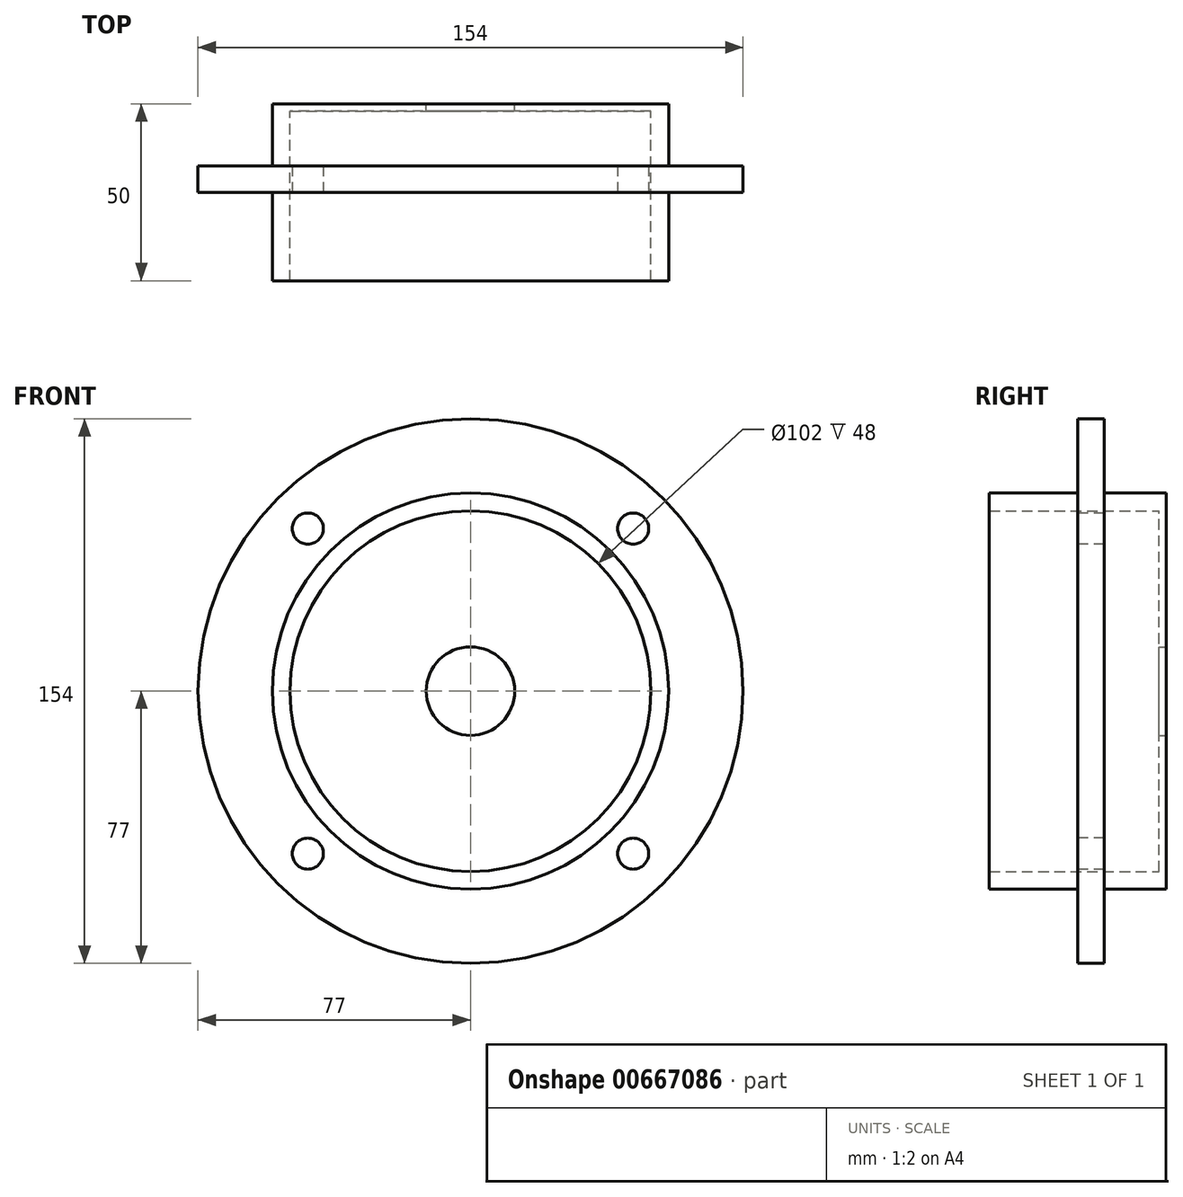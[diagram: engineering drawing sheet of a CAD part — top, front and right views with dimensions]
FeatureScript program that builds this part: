
annotation { "Feature Type Name" : "Feature", "Feature Type Description" : "" }
export const myFeature = defineFeature(function(context is Context, id is Id, definition is map)
    precondition{}
    {
        {
            var Q0;
            Q0=qCreatedBy(makeId("Front.planeOp"),FACE);
            var sketch = newSketch(context, id + "F0", { "sketchPlane" : qUnion([Q0])});
            skCircle(sketch, "E0", {"center": v(0, 0) * mm, "radius": 77 * mm});
            skCircle(sketch, "E1", {"center": v(0, 0) * mm, "radius": 56 * mm});
            skCircle(sketch, "E2.0", {"center": v(0, 0) * mm, "radius": 51 * mm});
            skSolve(sketch);
        }
        {
            var Q0;
            Q0=makeQuery(id+"F0.imprint","IMPRINT",FACE,{"disambiguationData":[TD([[makeQuery(id+"F0.imprint","IMPRINT",EDGE,{"derivedFrom":sQuery(id+"F0.wireOp",EDGE,"E1")}),1.0]])]});
            extrude(context, id + "F1", {"entities" : qUnion([Q0]), "depth" : 50 * mm, "offsetDistance" : 25 * mm});
        }
        {
            var Q0;
            Q0=makeQuery(id+"F0.imprint","IMPRINT",FACE,{"disambiguationData":[TD([[makeQuery(id+"F0.imprint","IMPRINT",EDGE,{"derivedFrom":sQuery(id+"F0.wireOp",EDGE,"E0")}),1.0]])]});
            extrude(context, id + "F2", {"entities" : qUnion([Q0]), "operationType" : NewBodyOperationType.ADD, "depth" : 25 * mm, "offsetDistance" : 25 * mm});
        }
        {
            var Q0;
            Q0=makeQuery(id+"F0.imprint","IMPRINT",FACE,{"disambiguationData":[TD([[makeQuery(id+"F0.imprint","IMPRINT",EDGE,{"derivedFrom":sQuery(id+"F0.wireOp",EDGE,"E0")}),1.0]])]});
            extrude(context, id + "F3", {"entities" : qUnion([Q0]), "operationType" : NewBodyOperationType.REMOVE, "depth" : 17.5 * mm, "offsetDistance" : 25 * mm});
        }
        {
            var Q0;
            Q0=makeQuery(id+"F2.opExtrude","CAP_FACE",FACE,{"disambiguationData":[OSD([sQuery(id+"F0.wireOp",EDGE,"E0"),sQuery(id+"F0.wireOp",EDGE,"E1")])],"isStart":false});
            var sketch = newSketch(context, id + "F4", { "sketchPlane" : qUnion([Q0])});
            skPoint(sketch, "E3", {"position": v(-45.96, 45.96) * mm});
            skPoint(sketch, "E4", {"position": v(45.96, 45.96) * mm});
            skPoint(sketch, "E5", {"position": v(45.96, -45.96) * mm});
            skPoint(sketch, "E6", {"position": v(-45.96, -45.96) * mm});
            skSolve(sketch);
        }
        {
            var Q0;
            Q0=sQuery(id+"F4.wireOp",VERTEX,"E3");
            var Q1;
            Q1=sQuery(id+"F4.wireOp",VERTEX,"E4");
            var Q2;
            Q2=sQuery(id+"F4.wireOp",VERTEX,"E5");
            var Q3;
            Q3=sQuery(id+"F4.wireOp",VERTEX,"E6");
            var Q4;
            Q4=makeQuery(id+"F1.opExtrude","SWEPT_BODY",BODY,{"disambiguationData":[OSD([sQuery(id+"F0.wireOp",EDGE,"E1"),sQuery(id+"F0.wireOp",EDGE,"E2.0")])]});
            hole(context, id + "F5", {"style" : HoleStyle.SIMPLE, "endStyle" : HoleEndStyle.THROUGH, "standardTappedOrClearance" : lookupTablePath({ "standard" : "ISO", "fit" : "Normal", "size" : "M8", "type" : "Clearance" }), "standardBlindInLast" : lookupTablePath({ "fit" : "Standard", "standard" : "ISO", "size" : "M8", "type" : "Clearance" }), "holeDiameter" : 8.8 * mm, "majorDiameter" : 5 * mm, "isTappedThrough" : true, "tappedDepth" : 12 * mm, "tapClearance" : 3, "locations" : qUnion([Q0, Q1, Q2, Q3]), "scope" : qUnion([Q4])});
        }
        {
            var Q0;
            Q0=qCreatedBy(makeId("Front.planeOp"),FACE);
            var sketch = newSketch(context, id + "F6", { "sketchPlane" : qUnion([Q0])});
            skCircle(sketch, "E7", {"center": v(0, 0) * mm, "radius": 12.5 * mm});
            skCircle(sketch, "E8.0", {"center": v(0, 0) * mm, "radius": 51 * mm});
            skSolve(sketch);
        }
        {
            var Q0;
            Q0=makeQuery(id+"F6.imprint","IMPRINT",FACE,{"disambiguationData":[TD([[makeQuery(id+"F6.imprint","IMPRINT",EDGE,{"derivedFrom":sQuery(id+"F6.wireOp",EDGE,"E7")}),-1.0]])]});
            extrude(context, id + "F7", {"entities" : qUnion([Q0]), "operationType" : NewBodyOperationType.ADD, "depth" : 2 * mm, "offsetDistance" : 25 * mm});
        }
    });
